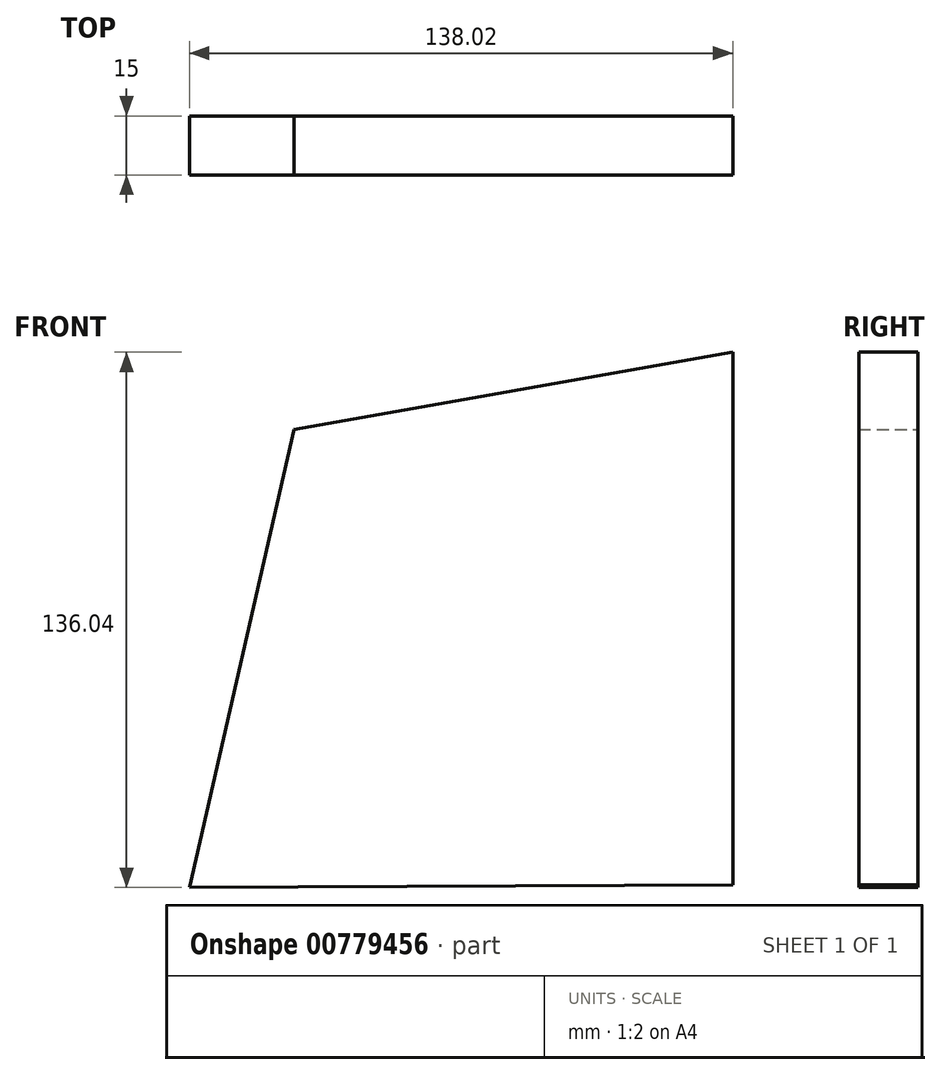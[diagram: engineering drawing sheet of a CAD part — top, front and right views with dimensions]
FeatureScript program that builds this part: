
annotation { "Feature Type Name" : "Feature", "Feature Type Description" : "" }
export const myFeature = defineFeature(function(context is Context, id is Id, definition is map)
    precondition{}
    {
        {
            var Q0;
            Q0=qCreatedBy(makeId("Front.planeOp"),FACE);
            var sketch = newSketch(context, id + "F0", { "sketchPlane" : qUnion([Q0])});
            skLineSegment(sketch, "E0", {"start": v(-75.09, -77.55) * mm, "end": v(-48.54, 38.8) * mm});
            skLineSegment(sketch, "E1", {"start": v(-48.54, 38.8) * mm, "end": v(62.93, 58.5) * mm});
            skLineSegment(sketch, "E2", {"start": v(62.93, 58.5) * mm, "end": v(62.93, -76.9) * mm});
            skLineSegment(sketch, "E3", {"start": v(62.93, -76.9) * mm, "end": v(-75.09, -77.55) * mm});
            skSolve(sketch);
        }
        {
            var Q0;
            Q0=makeQuery(id+"F0.imprint","IMPRINT",FACE,{"disambiguationData":[TD([[makeQuery(id+"F0.imprint","IMPRINT",EDGE,{"derivedFrom":sQuery(id+"F0.wireOp",EDGE,"E0")}),-1.0]])]});
            extrude(context, id + "F1", {"entities" : qUnion([Q0]), "depth" : 15 * mm, "offsetDistance" : 25 * mm});
        }
    });
